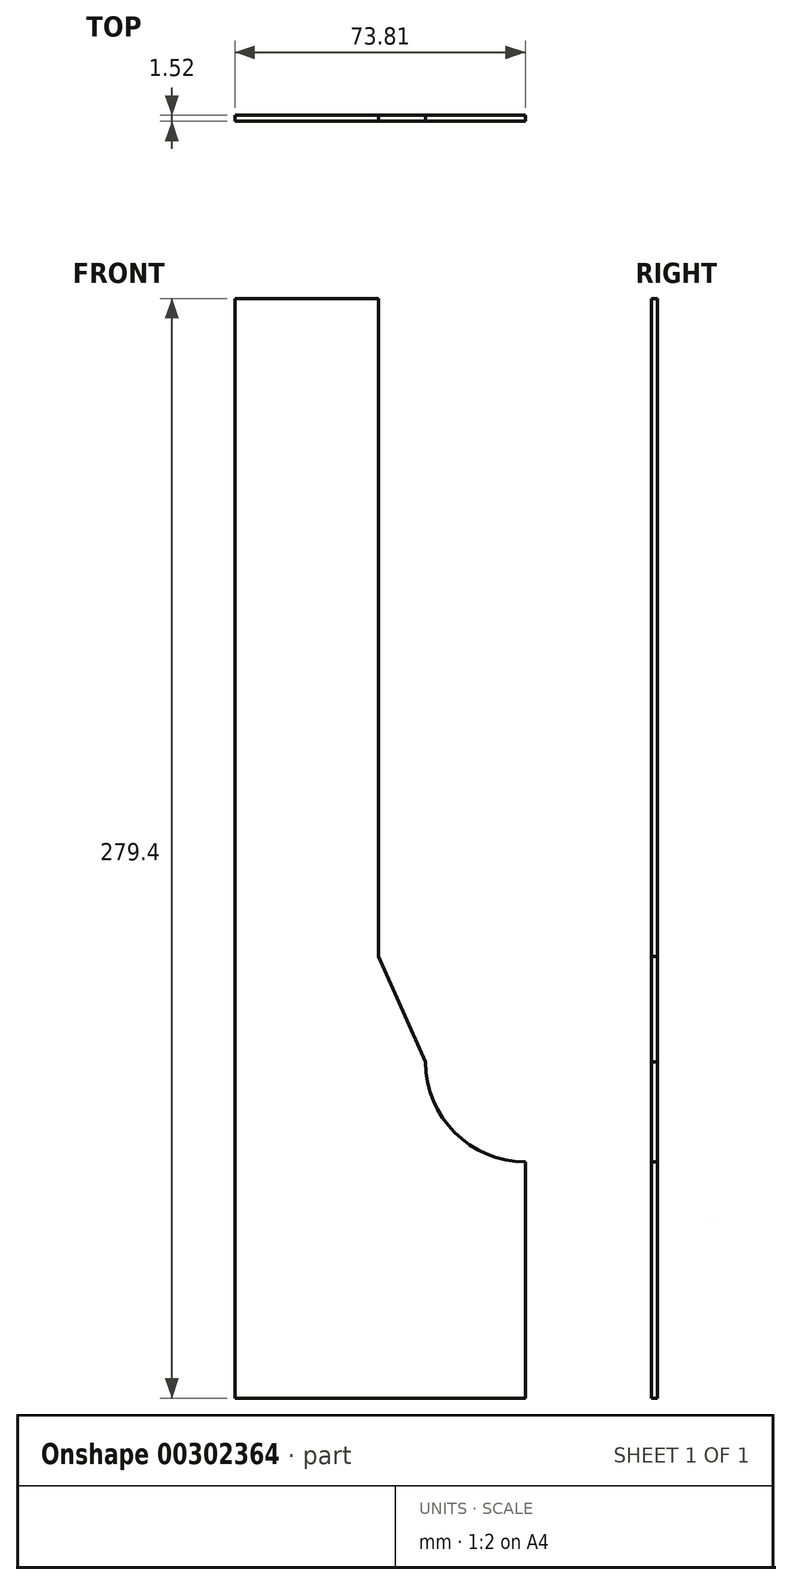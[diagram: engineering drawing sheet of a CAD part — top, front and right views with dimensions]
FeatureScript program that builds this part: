
annotation { "Feature Type Name" : "Feature", "Feature Type Description" : "" }
export const myFeature = defineFeature(function(context is Context, id is Id, definition is map)
    precondition{}
    {
        {
            var Q0;
            Q0=qCreatedBy(makeId("Front.planeOp"),FACE);
            var sketch = newSketch(context, id + "F0", { "sketchPlane" : qUnion([Q0])});
            skLineSegment(sketch, "E0", {"start": v(0, 0) * mm, "end": v(0, 279.4) * mm});
            skLineSegment(sketch, "E1", {"start": v(0, 279.4) * mm, "end": v(36.51, 279.4) * mm});
            skLineSegment(sketch, "E2", {"start": v(36.51, 279.4) * mm, "end": v(36.51, 112.25) * mm});
            skLineSegment(sketch, "E3", {"start": v(36.51, 112.25) * mm, "end": v(48.41, 85.42) * mm});
            skLineSegment(sketch, "E4", {"start": v(73.81, 60.02) * mm, "end": v(73.81, 0) * mm});
            skLineSegment(sketch, "E5", {"start": v(73.81, 0) * mm, "end": v(0, 0) * mm});
            skArc(sketch, "E6", {"start": v(48.41, 85.42) * mm, "mid": v(55.85, 67.46) * mm, "end": v(73.81, 60.02) * mm});
            skSolve(sketch);
        }
        {
            var Q0;
            Q0=makeQuery(id+"F0.imprint","IMPRINT",FACE,{"disambiguationData":[TD([[makeQuery(id+"F0.imprint","IMPRINT",EDGE,{"derivedFrom":sQuery(id+"F0.wireOp",EDGE,"E0")}),-1.0]])]});
            extrude(context, id + "F1", {"entities" : qUnion([Q0]), "oppositeDirection" : true, "depth" : 1.52 * mm});
        }
        {
            var Q0;
            Q0=makeQuery(id+"F1.opExtrude","SWEPT_BODY",BODY,{"disambiguationData":[OSD([sQuery(id+"F0.wireOp",EDGE,"E0"),sQuery(id+"F0.wireOp",EDGE,"E1"),sQuery(id+"F0.wireOp",EDGE,"E2"),sQuery(id+"F0.wireOp",EDGE,"E3"),sQuery(id+"F0.wireOp",EDGE,"E4"),sQuery(id+"F0.wireOp",EDGE,"E5"),sQuery(id+"F0.wireOp",EDGE,"E6")])]});
            transform(context, id + "F2", {"entities" : qUnion([Q0]), "transformType" : TransformType.TRANSLATION_3D, "dx" : 0 * mm, "dy" : 0 * mm, "dz" : 0 * mm, "makeCopy" : true});
        }
    });
